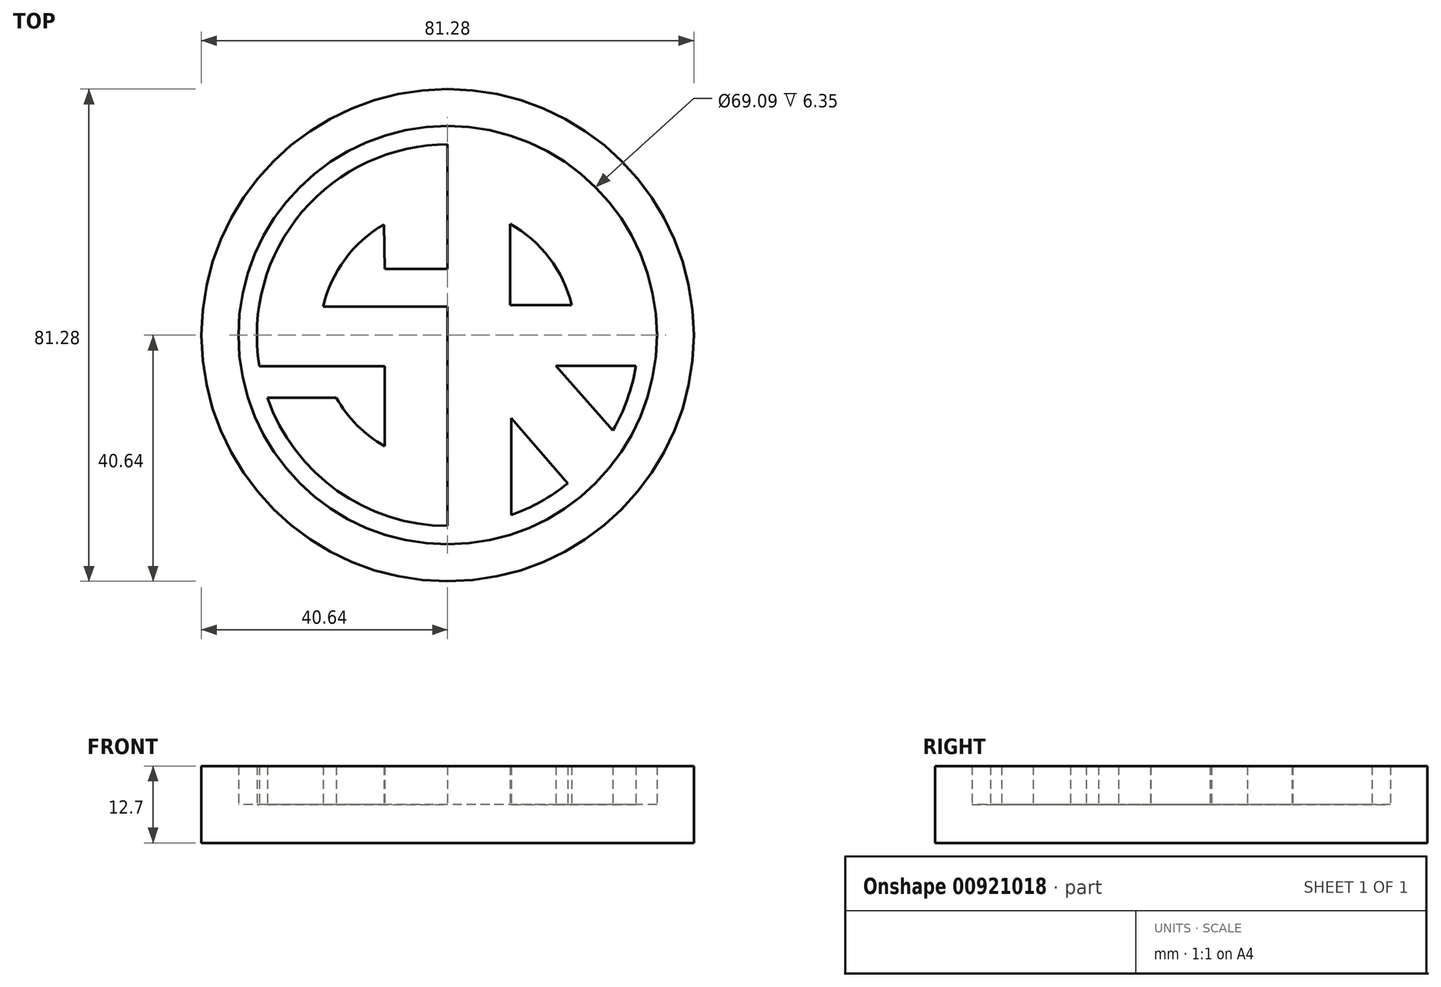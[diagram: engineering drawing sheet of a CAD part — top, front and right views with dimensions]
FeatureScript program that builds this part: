
annotation { "Feature Type Name" : "Feature", "Feature Type Description" : "" }
export const myFeature = defineFeature(function(context is Context, id is Id, definition is map)
    precondition{}
    {
        {
            var Q0;
            Q0=qCreatedBy(makeId("Top.planeOp"),FACE);
            var sketch = newSketch(context, id + "F0", { "sketchPlane" : qUnion([Q0])});
            skCircle(sketch, "E0", {"center": v(0, 0) * mm, "radius": 40.64 * mm});
            skCircle(sketch, "E1", {"center": v(0, 0) * mm, "radius": 34.54 * mm});
            skLineSegment(sketch, "E2", {"start": v(0, 31.5) * mm, "end": v(0, 10.92) * mm});
            skArc(sketch, "E3", {"start": v(-10.51, 18.27) * mm, "mid": v(-16.94, 12.55) * mm, "end": v(-20.55, 4.72) * mm});
            skLineSegment(sketch, "E4", {"start": v(0, 10.92) * mm, "end": v(-10.41, 10.92) * mm});
            skLineSegment(sketch, "E5", {"start": v(-10.51, 18.27) * mm, "end": v(-10.41, 10.92) * mm});
            skLineSegment(sketch, "E6", {"start": v(0, -31.5) * mm, "end": v(0, 4.72) * mm});
            skLineSegment(sketch, "E7", {"start": v(0, 4.72) * mm, "end": v(-20.55, 4.72) * mm});
            skLineSegment(sketch, "E8", {"start": v(-10.41, -18.33) * mm, "end": v(-10.41, -5.12) * mm});
            skLineSegment(sketch, "E9.trimOffspring", {"start": v(-10.41, -5.12) * mm, "end": v(-10.41, -18.33) * mm, "construction": true});
            skLineSegment(sketch, "E10", {"start": v(-10.41, -5.12) * mm, "end": v(-31.08, -5.12) * mm});
            skArc(sketch, "E11.trimOffspring", {"start": v(-18.37, -10.34) * mm, "mid": v(-14.94, -14.88) * mm, "end": v(-10.41, -18.33) * mm});
            skArc(sketch, "E12.trimOffspring", {"start": v(20.48, 5) * mm, "mid": v(16.8, 12.73) * mm, "end": v(10.35, 18.37) * mm});
            skLineSegment(sketch, "E13", {"start": v(-24.16, -10.34) * mm, "end": v(-24.16, -10.46) * mm, "construction": true});
            skLineSegment(sketch, "E14", {"start": v(-29.75, -10.34) * mm, "end": v(-18.37, -10.34) * mm});
            skArc(sketch, "E15.trimOffspring", {"start": v(10.52, -29.69) * mm, "mid": v(15.4, -27.48) * mm, "end": v(19.82, -24.48) * mm});
            skArc(sketch, "E16.trimOffspring", {"start": v(28.18, -14.06) * mm, "mid": v(29.98, -9.67) * mm, "end": v(31.09, -5.05) * mm});
            skPoint(sketch, "E17.orphan", {"position": v(10.41, 48.18) * mm});
            skLineSegment(sketch, "E18", {"start": v(10.35, 18.37) * mm, "end": v(10.35, 5) * mm});
            skLineSegment(sketch, "E19", {"start": v(20.48, 5) * mm, "end": v(10.35, 5) * mm});
            skLineSegment(sketch, "E20", {"start": v(10.52, -29.69) * mm, "end": v(10.52, -13.68) * mm});
            skLineSegment(sketch, "E21", {"start": v(10.52, -13.68) * mm, "end": v(19.82, -24.48) * mm});
            skLineSegment(sketch, "E22", {"start": v(31.09, -5.05) * mm, "end": v(17.88, -5.05) * mm});
            skArc(sketch, "E23", {"start": v(0, 31.5) * mm, "mid": v(-24.01, 20.38) * mm, "end": v(-31.08, -5.12) * mm});
            skLineSegment(sketch, "E24", {"start": v(17.88, -5.05) * mm, "end": v(27.3, -15.7) * mm});
            skArc(sketch, "E25.trimOffspring", {"start": v(27.3, -15.7) * mm, "mid": v(29.68, -10.55) * mm, "end": v(31.09, -5.05) * mm});
            skArc(sketch, "E26.trimOffspring", {"start": v(-29.75, -10.34) * mm, "mid": v(-18.25, -25.67) * mm, "end": v(0, -31.5) * mm});
            skPoint(sketch, "E27.end.orphan", {"position": v(10.41, 0) * mm});
            skSolve(sketch);
        }
        {
            var Q0;
            Q0=makeQuery(id+"F0.imprint","IMPRINT",FACE,{"disambiguationData":[TD([[makeQuery(id+"F0.imprint","IMPRINT",EDGE,{"derivedFrom":sQuery(id+"F0.wireOp",EDGE,"E1")}),1.0]])]});
            extrude(context, id + "F1", {"entities" : qUnion([Q0]), "depth" : 6.35 * mm, "offsetDistance" : 25.4 * mm});
        }
        {
            var Q0;
            Q0=makeQuery(id+"F0.imprint","IMPRINT",FACE,{"disambiguationData":[TD([[makeQuery(id+"F0.imprint","IMPRINT",EDGE,{"derivedFrom":sQuery(id+"F0.wireOp",EDGE,"E2")}),-1.0]])]});
            var Q1;
            Q1=makeQuery(id+"F0.imprint","IMPRINT",FACE,{"disambiguationData":[TD([[makeQuery(id+"F0.imprint","IMPRINT",EDGE,{"derivedFrom":sQuery(id+"F0.wireOp",EDGE,"E20")}),-1.0]])]});
            var Q2;
            Q2=makeQuery(id+"F0.imprint","IMPRINT",FACE,{"disambiguationData":[TD([[makeQuery(id+"F0.imprint","IMPRINT",EDGE,{"derivedFrom":sQuery(id+"F0.wireOp",EDGE,"E12.trimOffspring")}),1.0]])]});
            var Q3;
            {var subQ0=sQuery(id+"F0.wireOp",EDGE,"E22");Q3=makeQuery(id+"F0.imprint","IMPRINT",FACE,{"disambiguationData":[TD([[makeQuery(id+"F0.imprint","IMPRINT",EDGE,{"derivedFrom":subQ0}),1.0]])]});}
            var Q4;
            Q4=makeQuery(id+"F0.imprint","IMPRINT",FACE,{"disambiguationData":[TD([[makeQuery(id+"F0.imprint","IMPRINT",EDGE,{"derivedFrom":sQuery(id+"F0.wireOp",EDGE,"E0")}),1.0]])]});
            extrude(context, id + "F2", {"entities" : qUnion([Q0, Q1, Q2, Q3, Q4]), "operationType" : NewBodyOperationType.ADD, "depth" : 12.7 * mm, "offsetDistance" : 25.4 * mm});
        }
    });
